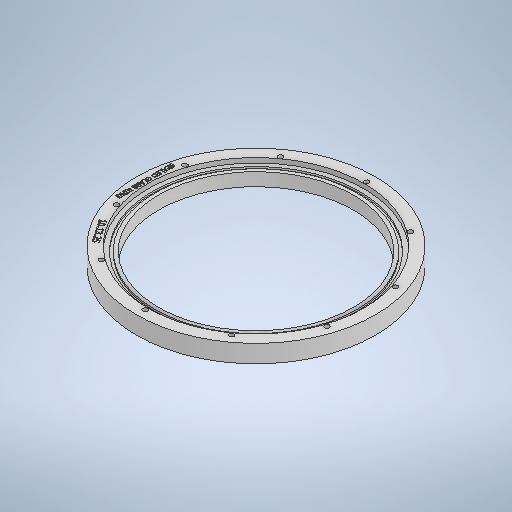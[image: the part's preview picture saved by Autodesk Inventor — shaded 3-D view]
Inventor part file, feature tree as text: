
AUTODESK INVENTOR PART (.ipt)
format: ipt  version: 2025 (Build 290162000, 162)  size: 818,176 bytes
history: native  units: mm
features: sketch x6, other x3, extrude x2, hole x1, pattern_circular x1
ambient origin geometry x8: Origin, YZ Plane, XZ Plane, XY Plane, X Axis, Y Axis, Z Axis, Center Point
bodies: Solid1 (feature_tree)
feature tree (13):
  extrude  "Ring"  Depth=270.0mm
  extrude  "Glass Seat"  Depth=20.0mm
  hole  "Holes"  [1 undecoded]
  pattern_circular  "Circular Pattern1"  Count=10 Angle=360.0deg
  other  "LABEL"
  other  "DATE"
  other  "Seal Grooves"
  sketch  "Sketch1"  dims[d0=220.0mm d1=270.0mm]
  sketch  "Sketch2"  dims[d2=20.0mm d3=0.0mm d4=244.0mm]
  sketch  "Sketch3"  dims[d5=5.3mm d6=0.0mm]
  sketch  "Sketch4"  dims[d7=5.5mm d8=6.0mm d9=4.0mm d10=2.0mm d11=90.0deg d12=8.0mm d13=20.594885mm d14=125.0mm d15=100.0mm d16=360.0deg]
  sketch  "Sketch6"  dims[d18=1.0mm d19=0.0mm]
  sketch  "Sketch7"  dims[d27=1.0mm d28=0.0mm d29=3.0mm d30=2.0mm d31=114.0mm d32=360.0deg d33=3.0mm d34=2.5mm]
note: 1 required parameter value undecoded (feature->parameter linkage not recoverable at this tier; creation-order binding heuristic only, values carry confidence <= 0.55)
